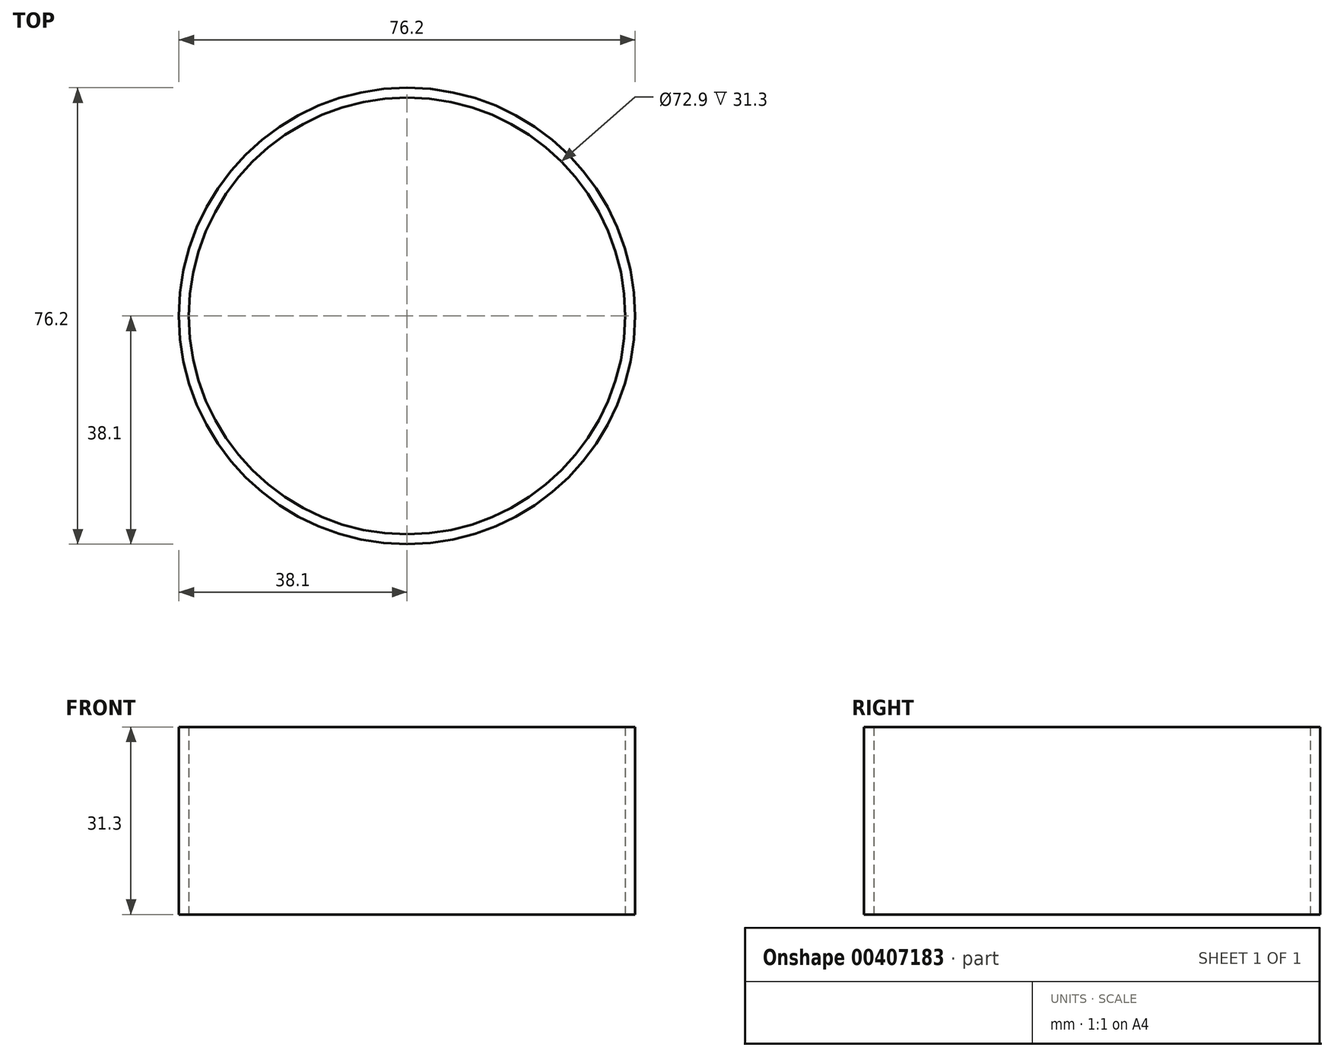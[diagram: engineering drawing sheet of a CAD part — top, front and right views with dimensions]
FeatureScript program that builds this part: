
annotation { "Feature Type Name" : "Feature", "Feature Type Description" : "" }
export const myFeature = defineFeature(function(context is Context, id is Id, definition is map)
    precondition{}
    {
        {
            var Q0;
            Q0=qCreatedBy(makeId("Top.planeOp"),FACE);
            var sketch = newSketch(context, id + "F0", { "sketchPlane" : qUnion([Q0])});
            skCircle(sketch, "E0", {"center": v(0, 0) * mm, "radius": 38.1 * mm});
            skCircle(sketch, "E1", {"center": v(0, 0) * mm, "radius": 36.45 * mm});
            skSolve(sketch);
        }
        {
            var Q0;
            Q0 = qSketchRegion(id + "F0", true);
            extrude(context, id + "F1", {"entities" : qUnion([Q0]), "depth" : 31.3 * mm});
        }
    });
